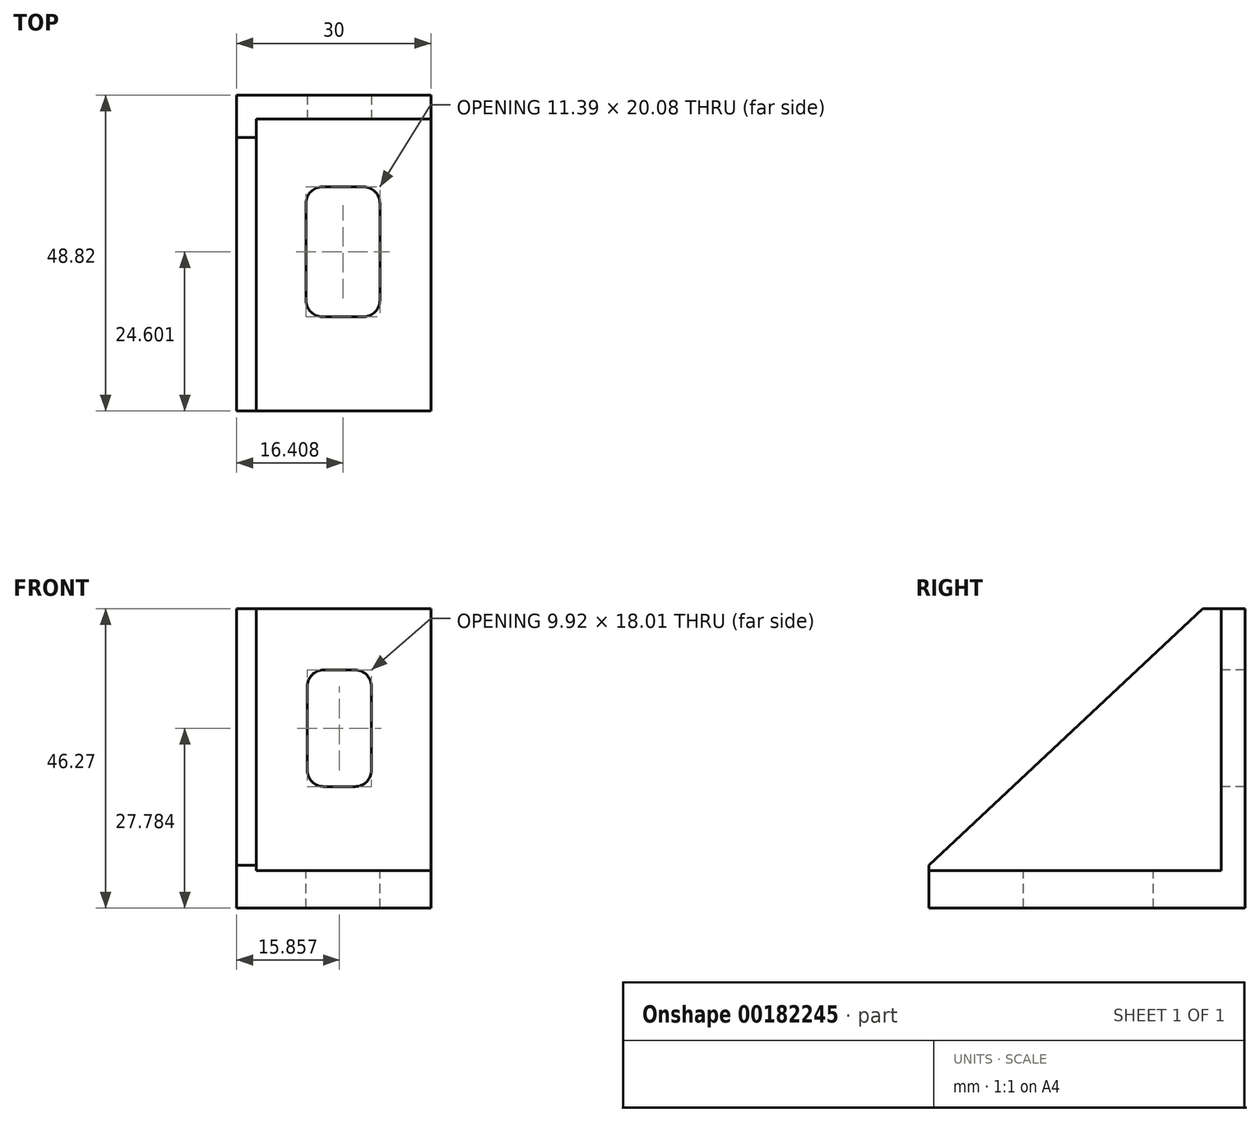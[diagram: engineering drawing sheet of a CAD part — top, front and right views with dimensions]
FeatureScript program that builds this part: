
annotation { "Feature Type Name" : "Feature", "Feature Type Description" : "" }
export const myFeature = defineFeature(function(context is Context, id is Id, definition is map)
    precondition{}
    {
        {
            var Q0;
            Q0=qCreatedBy(makeId("Right.planeOp"),FACE);
            var sketch = newSketch(context, id + "F0", { "sketchPlane" : qUnion([Q0])});
            skLineSegment(sketch, "E0", {"start": v(0, 0) * mm, "end": v(48.82, 0) * mm});
            skLineSegment(sketch, "E1", {"start": v(48.82, 0) * mm, "end": v(48.82, 46.27) * mm});
            skLineSegment(sketch, "E2", {"start": v(48.82, 46.27) * mm, "end": v(42.24, 46.27) * mm});
            skLineSegment(sketch, "E3", {"start": v(42.24, 46.27) * mm, "end": v(0, 6.6) * mm});
            skLineSegment(sketch, "E4", {"start": v(0, 6.6) * mm, "end": v(0, 0) * mm});
            skSolve(sketch);
        }
        {
            var Q0;
            Q0=makeQuery(id+"F0.imprint","IMPRINT",FACE,{"disambiguationData":[TD([[makeQuery(id+"F0.imprint","IMPRINT",EDGE,{"derivedFrom":sQuery(id+"F0.wireOp",EDGE,"E0")}),1.0]])]});
            extrude(context, id + "F1", {"entities" : qUnion([Q0]), "oppositeDirection" : true, "depth" : 30 * mm});
        }
        {
            var Q0;
            Q0=qCreatedBy(makeId("Right.planeOp"),FACE);
            var sketch = newSketch(context, id + "F2", { "sketchPlane" : qUnion([Q0])});
            skLineSegment(sketch, "E5", {"start": v(45.11, 61.9) * mm, "end": v(45.11, 5.81) * mm});
            skLineSegment(sketch, "E6", {"start": v(45.11, 5.81) * mm, "end": v(-13.77, 5.81) * mm});
            skLineSegment(sketch, "E7", {"start": v(-13.77, 5.81) * mm, "end": v(45.11, 61.9) * mm});
            skSolve(sketch);
        }
        {
            var Q0;
            Q0=makeQuery(id+"F2.imprint","IMPRINT",FACE,{"disambiguationData":[TD([[makeQuery(id+"F2.imprint","IMPRINT",EDGE,{"derivedFrom":sQuery(id+"F2.wireOp",EDGE,"E5")}),-1.0]])]});
            extrude(context, id + "F3", {"entities" : qUnion([Q0]), "oppositeDirection" : true, "depth" : 27 * mm});
        }
        {
            var Q0;
            Q0=makeQuery(id+"F3.opExtrude","SWEPT_BODY",BODY,{"disambiguationData":[OSD([sQuery(id+"F2.wireOp",EDGE,"E5"),sQuery(id+"F2.wireOp",EDGE,"E6"),sQuery(id+"F2.wireOp",EDGE,"E7")])]});
            var Q1;
            Q1=makeQuery(id+"F1.opExtrude","SWEPT_BODY",BODY,{"disambiguationData":[OSD([sQuery(id+"F0.wireOp",EDGE,"E0"),sQuery(id+"F0.wireOp",EDGE,"E1"),sQuery(id+"F0.wireOp",EDGE,"E2"),sQuery(id+"F0.wireOp",EDGE,"E3"),sQuery(id+"F0.wireOp",EDGE,"E4")])]});
            booleanBodies(context, id + "F4", {"operationType" : BooleanOperationType.SUBTRACTION, "tools" : qUnion([Q0]), "targets" : qUnion([Q1])});
        }
        {
            var Q0;
            Q0=makeQuery(id+"F4.opBoolean","COPY",FACE,{"derivedFrom":makeQuery(id+"F3.opExtrude","SWEPT_FACE",FACE,{"disambiguationData":[OSD([sQuery(id+"F2.wireOp",EDGE,"E6")])]})});
            var sketch = newSketch(context, id + "F5", { "sketchPlane" : qUnion([Q0])});
            skLineSegment(sketch, "E8.bottom", {"start": v(-16.75, 34.64) * mm, "end": v(-10.44, 34.64) * mm});
            skLineSegment(sketch, "E8.top", {"start": v(-16.75, 14.56) * mm, "end": v(-10.44, 14.56) * mm});
            skLineSegment(sketch, "E8.left", {"start": v(-19.29, 32.1) * mm, "end": v(-19.29, 17.1) * mm});
            skLineSegment(sketch, "E8.right", {"start": v(-7.9, 32.1) * mm, "end": v(-7.9, 17.1) * mm});
            skPoint(sketch, "E9.visualSharp", {"position": v(-19.29, 34.64) * mm});
            skArc(sketch, "E9.filletArc", {"start": v(-16.75, 34.64) * mm, "mid": v(-18.55, 33.9) * mm, "end": v(-19.29, 32.1) * mm});
            skPoint(sketch, "E10.visualSharp", {"position": v(-7.9, 34.64) * mm});
            skArc(sketch, "E10.filletArc", {"start": v(-7.9, 32.1) * mm, "mid": v(-8.64, 33.9) * mm, "end": v(-10.44, 34.64) * mm});
            skPoint(sketch, "E11.visualSharp", {"position": v(-7.9, 14.56) * mm});
            skArc(sketch, "E11.filletArc", {"start": v(-10.44, 14.56) * mm, "mid": v(-8.64, 15.3) * mm, "end": v(-7.9, 17.1) * mm});
            skPoint(sketch, "E12.visualSharp", {"position": v(-19.29, 14.56) * mm});
            skArc(sketch, "E12.filletArc", {"start": v(-19.29, 17.1) * mm, "mid": v(-18.55, 15.3) * mm, "end": v(-16.75, 14.56) * mm});
            skSolve(sketch);
        }
        {
            var Q0;
            Q0=qSketchRegion(id+"F5",true);
            extrude(context, id + "F6", {"entities" : qUnion([Q0]), "operationType" : NewBodyOperationType.REMOVE, "endBound" : BoundingType.UP_TO_NEXT, "oppositeDirection" : true, "depth" : 25.4 * mm});
        }
        {
            var Q0;
            Q0=makeQuery(id+"F4.opBoolean","COPY",FACE,{"derivedFrom":makeQuery(id+"F3.opExtrude","SWEPT_FACE",FACE,{"disambiguationData":[OSD([sQuery(id+"F2.wireOp",EDGE,"E5")])]})});
            var sketch = newSketch(context, id + "F7", { "sketchPlane" : qUnion([Q0])});
            skLineSegment(sketch, "E13.bottom", {"start": v(-16.57, 36.79) * mm, "end": v(-11.72, 36.79) * mm});
            skLineSegment(sketch, "E13.top", {"start": v(-16.57, 18.78) * mm, "end": v(-11.72, 18.78) * mm});
            skLineSegment(sketch, "E13.left", {"start": v(-19.1, 34.25) * mm, "end": v(-19.1, 21.32) * mm});
            skLineSegment(sketch, "E13.right", {"start": v(-9.18, 34.25) * mm, "end": v(-9.18, 21.32) * mm});
            skPoint(sketch, "E14.visualSharp", {"position": v(-19.1, 36.79) * mm});
            skArc(sketch, "E14.filletArc", {"start": v(-16.57, 36.79) * mm, "mid": v(-18.36, 36.04) * mm, "end": v(-19.1, 34.25) * mm});
            skPoint(sketch, "E15.visualSharp", {"position": v(-9.18, 36.79) * mm});
            skArc(sketch, "E15.filletArc", {"start": v(-9.18, 34.25) * mm, "mid": v(-9.93, 36.04) * mm, "end": v(-11.72, 36.79) * mm});
            skPoint(sketch, "E16.visualSharp", {"position": v(-9.18, 18.78) * mm});
            skArc(sketch, "E16.filletArc", {"start": v(-11.72, 18.78) * mm, "mid": v(-9.93, 19.52) * mm, "end": v(-9.18, 21.32) * mm});
            skPoint(sketch, "E17.visualSharp", {"position": v(-19.1, 18.78) * mm});
            skArc(sketch, "E17.filletArc", {"start": v(-19.1, 21.32) * mm, "mid": v(-18.36, 19.52) * mm, "end": v(-16.57, 18.78) * mm});
            skSolve(sketch);
        }
        {
            var Q0;
            Q0=qSketchRegion(id+"F7",true);
            extrude(context, id + "F8", {"entities" : qUnion([Q0]), "operationType" : NewBodyOperationType.REMOVE, "endBound" : BoundingType.UP_TO_NEXT, "oppositeDirection" : true, "depth" : 25.4 * mm});
        }
    });
